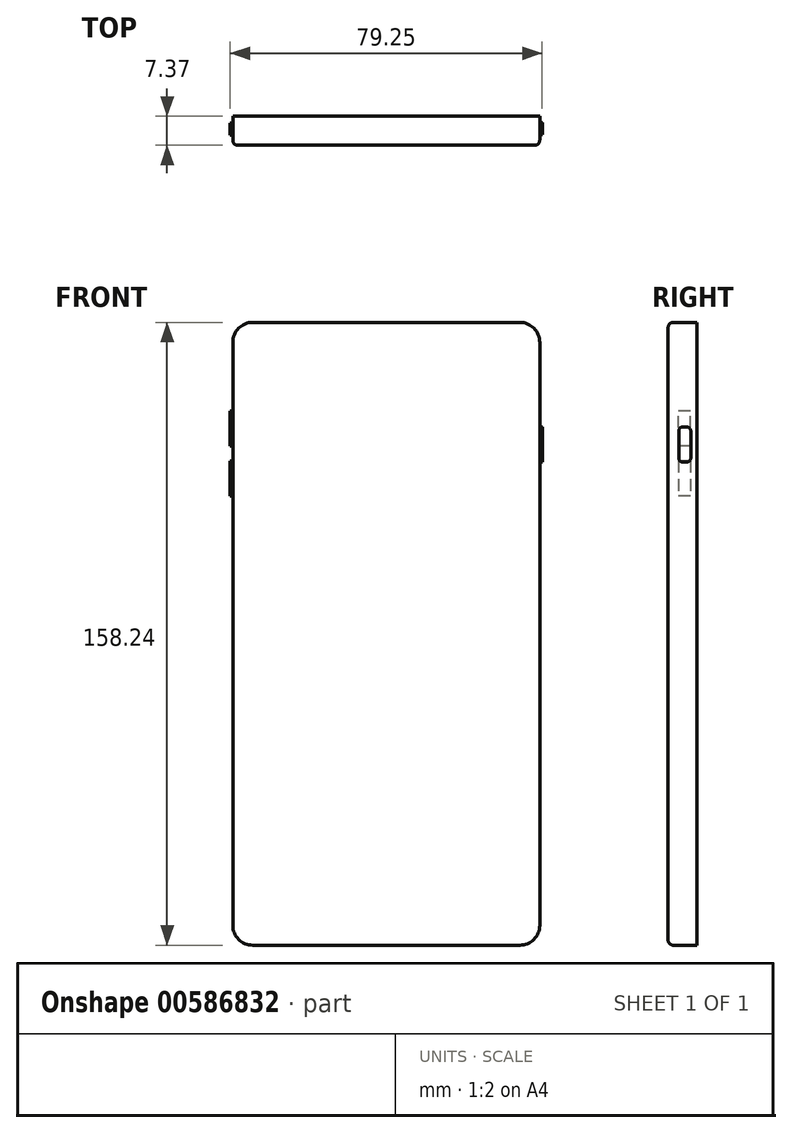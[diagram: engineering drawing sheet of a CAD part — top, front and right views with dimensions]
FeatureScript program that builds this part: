
annotation { "Feature Type Name" : "Feature", "Feature Type Description" : "" }
export const myFeature = defineFeature(function(context is Context, id is Id, definition is map)
    precondition{}
    {
        {
            var Q0;
            Q0=qCreatedBy(makeId("Front.planeOp"),FACE);
            var sketch = newSketch(context, id + "F0", { "sketchPlane" : qUnion([Q0])});
            skLineSegment(sketch, "E0", {"start": v(0, 5.08) * mm, "end": v(0, 153.16) * mm});
            skLineSegment(sketch, "E1", {"start": v(5.08, 158.24) * mm, "end": v(72.9, 158.24) * mm});
            skLineSegment(sketch, "E2", {"start": v(77.98, 153.16) * mm, "end": v(77.98, 5.08) * mm});
            skLineSegment(sketch, "E3", {"start": v(72.9, 0) * mm, "end": v(5.08, 0) * mm});
            skPoint(sketch, "E4.visualSharp", {"position": v(0, 158.24) * mm});
            skArc(sketch, "E4.filletArc", {"start": v(5.08, 158.24) * mm, "mid": v(1.49, 156.75) * mm, "end": v(0, 153.16) * mm});
            skPoint(sketch, "E5.visualSharp", {"position": v(77.98, 158.24) * mm});
            skArc(sketch, "E5.filletArc", {"start": v(77.98, 153.16) * mm, "mid": v(76.5, 156.75) * mm, "end": v(72.9, 158.24) * mm});
            skPoint(sketch, "E6.visualSharp", {"position": v(0, 0) * mm});
            skArc(sketch, "E6.filletArc", {"start": v(0, 5.08) * mm, "mid": v(1.49, 1.49) * mm, "end": v(5.08, 0) * mm});
            skPoint(sketch, "E7.visualSharp", {"position": v(77.98, 0) * mm});
            skArc(sketch, "E7.filletArc", {"start": v(72.9, 0) * mm, "mid": v(76.5, 1.49) * mm, "end": v(77.98, 5.08) * mm});
            skSolve(sketch);
        }
        {
            var Q0;
            Q0=makeQuery(id+"F0.imprint","IMPRINT",FACE,{"disambiguationData":[TD([[makeQuery(id+"F0.imprint","IMPRINT",EDGE,{"derivedFrom":sQuery(id+"F0.wireOp",EDGE,"E0")}),-1.0]])]});
            extrude(context, id + "F1", {"entities" : qUnion([Q0]), "depth" : 7.37 * mm, "offsetDistance" : 25.4 * mm});
        }
        {
            var Q0;
            Q0=makeQuery(id+"F1.opExtrude","CAP_EDGE",EDGE,{"disambiguationData":[OSD([sQuery(id+"F0.wireOp",EDGE,"E3")])],"isStart":false});
            fillet(context, id + "F2", {"entities" : qUnion([Q0]), "radius" : 1.27 * mm, "tangentPropagation" : true, "allowEdgeOverflow" : false});
        }
        {
            var Q0;
            Q0=makeQuery(id+"F1.opExtrude","SWEPT_FACE",FACE,{"disambiguationData":[OSD([sQuery(id+"F0.wireOp",EDGE,"E2")])]});
            var sketch = newSketch(context, id + "F3", { "sketchPlane" : qUnion([Q0])});
            skLineSegment(sketch, "E8.bottom", {"start": v(-3.67, 131.65) * mm, "end": v(-2.66, 131.65) * mm});
            skLineSegment(sketch, "E8.top", {"start": v(-3.67, 122.76) * mm, "end": v(-2.66, 122.76) * mm});
            skLineSegment(sketch, "E8.left", {"start": v(-4.7, 130.63) * mm, "end": v(-4.7, 123.77) * mm});
            skLineSegment(sketch, "E8.right", {"start": v(-1.64, 130.63) * mm, "end": v(-1.64, 123.77) * mm});
            skPoint(sketch, "E9.visualSharp", {"position": v(-4.7, 131.65) * mm});
            skArc(sketch, "E9.filletArc", {"start": v(-3.67, 131.65) * mm, "mid": v(-4.4, 131.35) * mm, "end": v(-4.7, 130.63) * mm});
            skPoint(sketch, "E10.visualSharp", {"position": v(-1.64, 131.65) * mm});
            skArc(sketch, "E10.filletArc", {"start": v(-1.64, 130.63) * mm, "mid": v(-1.94, 131.35) * mm, "end": v(-2.66, 131.65) * mm});
            skPoint(sketch, "E11.visualSharp", {"position": v(-1.64, 122.76) * mm});
            skArc(sketch, "E11.filletArc", {"start": v(-2.66, 122.76) * mm, "mid": v(-1.94, 123.06) * mm, "end": v(-1.64, 123.77) * mm});
            skPoint(sketch, "E12.visualSharp", {"position": v(-4.7, 122.76) * mm});
            skArc(sketch, "E12.filletArc", {"start": v(-4.7, 123.77) * mm, "mid": v(-4.4, 123.06) * mm, "end": v(-3.67, 122.76) * mm});
            skSolve(sketch);
        }
        {
            var Q0;
            Q0=makeQuery(id+"F3.imprint","IMPRINT",FACE,{"disambiguationData":[TD([[makeQuery(id+"F3.imprint","IMPRINT",EDGE,{"derivedFrom":sQuery(id+"F3.wireOp",EDGE,"E8.bottom")}),-1.0]])]});
            extrude(context, id + "F4", {"entities" : qUnion([Q0]), "operationType" : NewBodyOperationType.ADD, "depth" : 0.64 * mm, "offsetDistance" : 25.4 * mm});
        }
        {
            var Q0;
            Q0=makeQuery(id+"F1.opExtrude","SWEPT_FACE",FACE,{"disambiguationData":[OSD([sQuery(id+"F0.wireOp",EDGE,"E0")])]});
            var sketch = newSketch(context, id + "F5", { "sketchPlane" : qUnion([Q0])});
            skLineSegment(sketch, "E13.bottom", {"start": v(1.7, 123.07) * mm, "end": v(4.75, 123.07) * mm});
            skLineSegment(sketch, "E13.top", {"start": v(1.7, 114.18) * mm, "end": v(4.75, 114.18) * mm});
            skLineSegment(sketch, "E13.left", {"start": v(1.7, 123.07) * mm, "end": v(1.7, 114.18) * mm});
            skLineSegment(sketch, "E13.right", {"start": v(4.75, 123.07) * mm, "end": v(4.75, 114.18) * mm});
            skLineSegment(sketch, "E14.bottom", {"start": v(1.7, 126.88) * mm, "end": v(4.75, 126.88) * mm});
            skLineSegment(sketch, "E14.top", {"start": v(1.7, 135.77) * mm, "end": v(4.75, 135.77) * mm});
            skLineSegment(sketch, "E14.left", {"start": v(1.7, 126.88) * mm, "end": v(1.7, 135.77) * mm});
            skLineSegment(sketch, "E14.right", {"start": v(4.75, 126.88) * mm, "end": v(4.75, 135.77) * mm});
            skSolve(sketch);
        }
        {
            var Q0;
            Q0=makeQuery(id+"F5.imprint","IMPRINT",FACE,{"disambiguationData":[TD([[makeQuery(id+"F5.imprint","IMPRINT",EDGE,{"derivedFrom":sQuery(id+"F5.wireOp",EDGE,"E14.bottom")}),1.0]])]});
            var Q1;
            Q1=makeQuery(id+"F5.imprint","IMPRINT",FACE,{"disambiguationData":[TD([[makeQuery(id+"F5.imprint","IMPRINT",EDGE,{"derivedFrom":sQuery(id+"F5.wireOp",EDGE,"E13.bottom")}),-1.0]])]});
            extrude(context, id + "F6", {"entities" : qUnion([Q0, Q1]), "operationType" : NewBodyOperationType.ADD, "depth" : 0.64 * mm, "offsetDistance" : 25.4 * mm});
        }
    });
